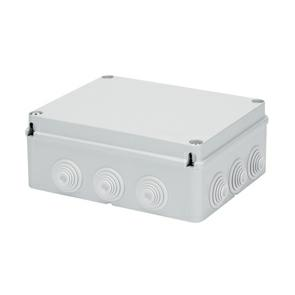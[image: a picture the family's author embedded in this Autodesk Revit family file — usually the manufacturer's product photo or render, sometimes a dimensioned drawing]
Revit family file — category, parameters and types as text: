
# Revit family: Building-SurfaceMountingEnclosures-GEWISS-44CE-JUNCTION-BOXES-WALL-MOUNTING_12HOLES
name_source: partatom
category: Apparecchi elettrici
revit_build: Autodesk Revit 2016 (Build: 20161004_0715(x64)
units: mm (PartAtom-declared; Revit-internal decimal feet)

## family parameters
Condiviso = No
Host = Superficie
Mantenere orientamento annotazione = Sì
Numero OmniClass = 23.80.30.14.24
Punto di calcolo locali = Sì
Quota connettore circolare = Usa diametro
Taglio con vuoti quando caricato = No
Tipo di parte = Normale
Titolo OmniClass = Junction Boxes

## types (1)
- Building-SurfaceMountingEnclosures-GEWISS-44CE-JUNCTION-BOXES-WALL-MOUNTING_12HOLES
    Accessories for insulation restoring = GW44621, GW44623
    Application = Special uses
    Carico apparente = 0 VA
    Catalogue = BUILDING
    Catalogue Range = 44 CE
    Classificazione = Other
    Colour = Grey RAL 7035
    Coperchio = GEWISS COPERCHIO
    Descrizione = JUNCT.BOX GL.380X300X120 IP55 GWT960
    Dettaglio = Elemento di dettaglio - 44CE-12IN : 380X300X120
    Diametro connessioni = 30 mm  [stored 0.0984252 ft]
    EAN code = 8011564243859
    Electrocod = 02210
    Entries No. holes / Ã˜ = 12 / 48
    Glow Wire Test = 960°C
    IDF = b295e427-0e84-407e-92a9-23a04096eefe
    IDT = 3c1c6504-ca7d-486c-980e-388c46ab8b09
    IP degree = IP55
    Immagine tipo = GW44060.jpg
    Insulation class = II (according to IEC 61140 standards)
    Internal dim. LxHxD (mm) = 380x300x120
    Larghezza_interna = 380 mm
    Lid = Plain screwed
    Lid screws (no. and type) = 4 insul. sealable hinged
    Lunghezza_interna = 300 mm
    Material = Technopolymer GWPLAST 75
    Modello = GW44060
    Operating temperature = -25 +60 °C
    Produttore = GEWISS S.p.A.
    Prospetto di default = 1219 mm
    SEO = Box
    Scatola = GEWISS SCATOLA
    Shock resistance = IK08
    Spessore = 120 mm  [stored 0.393701 ft]
    Technical sheet = https://www.gewiss.com
    Thermo-pressure with ball = 85
    Torque screws tightening = 1,8NM
    URL = https://www.gewiss.com
    Version file RFA = 18.0
    Voltaggio_x = 0 V
    Walls = With cable glands
    raggio = 15 mm  [stored 0.0492126 ft]

note: source unit labels omitted for Thermo-pressure with ball — the stored unit's dimension contradicts the parameter name (converter mislabeling)

note: [stored X ft] marks values corroborated as IEEE doubles in the binary element streams (Revit-internal decimal feet)

## geometry (parser evidence)
native form markers: Sweep x2
no freeform markers — native parametric forms only
